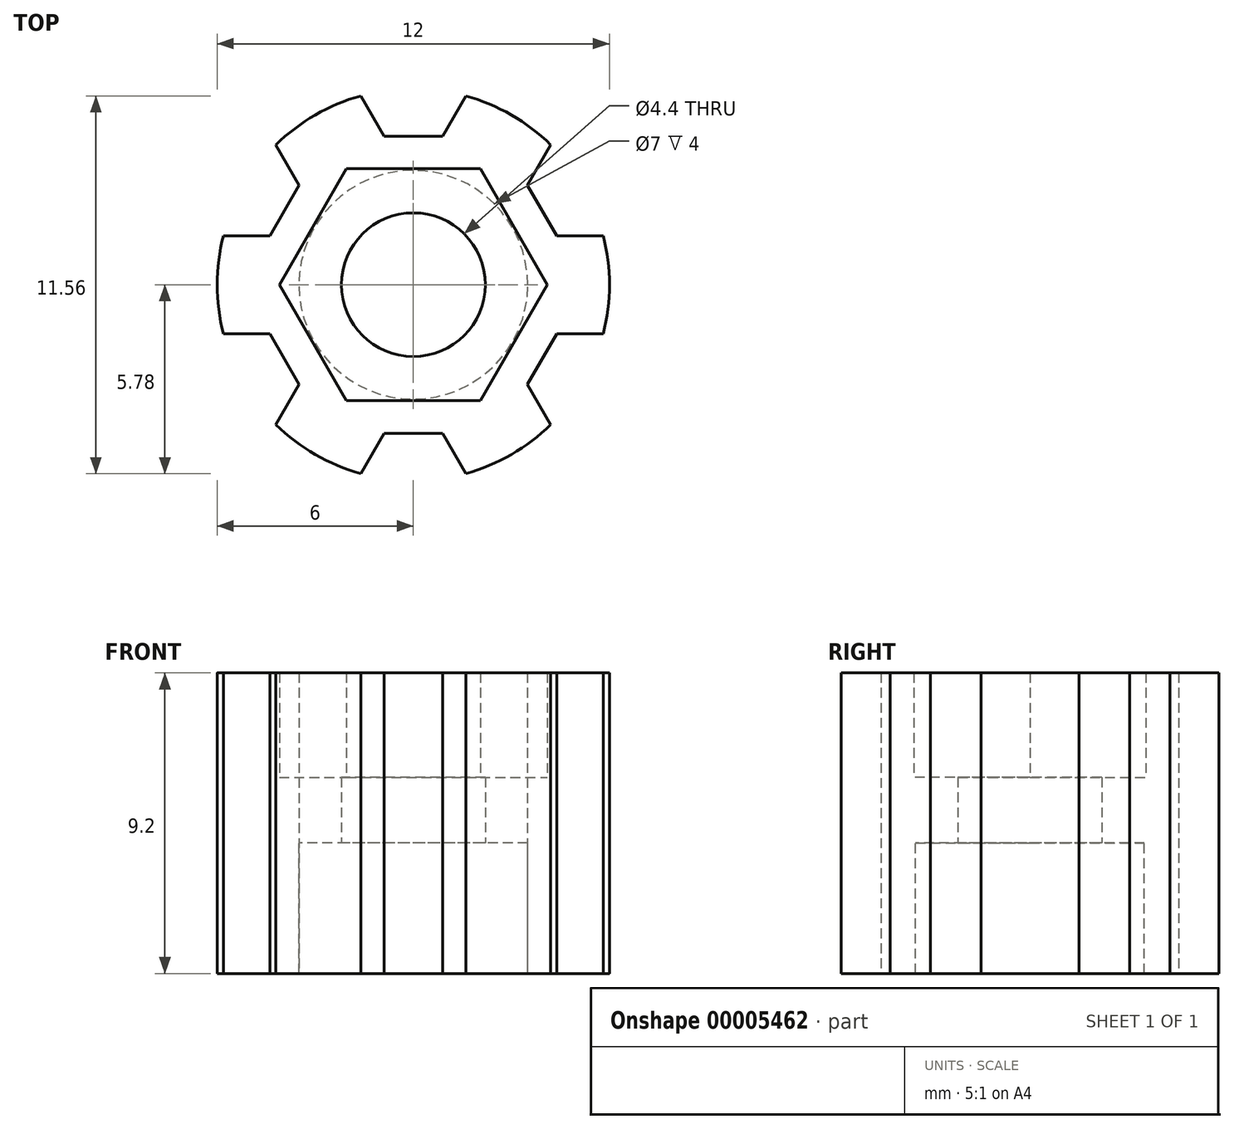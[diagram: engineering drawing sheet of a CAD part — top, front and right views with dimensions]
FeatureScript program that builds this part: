
annotation { "Feature Type Name" : "Feature", "Feature Type Description" : "" }
export const myFeature = defineFeature(function(context is Context, id is Id, definition is map)
    precondition{}
    {
        {
            var Q0;
            Q0=qCreatedBy(makeId("Top.planeOp"),FACE);
            var sketch = newSketch(context, id + "F0", { "sketchPlane" : qUnion([Q0])});
            skCircle(sketch, "E0.cCircle", {"center": v(0, 0) * mm, "radius": 3.55 * mm, "construction": true});
            skLineSegment(sketch, "E0.0", {"start": v(-2.05, 3.55) * mm, "end": v(2.05, 3.55) * mm});
            skLineSegment(sketch, "E0.1", {"start": v(2.05, 3.55) * mm, "end": v(4.1, 0) * mm});
            skLineSegment(sketch, "E0.2", {"start": v(4.1, 0) * mm, "end": v(2.05, -3.55) * mm});
            skLineSegment(sketch, "E0.3", {"start": v(2.05, -3.55) * mm, "end": v(-2.05, -3.55) * mm});
            skLineSegment(sketch, "E0.4", {"start": v(-2.05, -3.55) * mm, "end": v(-4.1, 0) * mm});
            skLineSegment(sketch, "E0.5", {"start": v(-4.1, 0) * mm, "end": v(-2.05, 3.55) * mm});
            skPoint(sketch, "E0.0.midPoint", {"position": v(0, 3.55) * mm});
            skCircle(sketch, "E1", {"center": v(0, 0) * mm, "radius": 2.2 * mm});
            skCircle(sketch, "E2", {"center": v(0, 0) * mm, "radius": 6 * mm});
            skLineSegment(sketch, "E3", {"start": v(-1.6, 5.78) * mm, "end": v(-0.9, 4.55) * mm});
            skLineSegment(sketch, "E4", {"start": v(-0.9, 4.55) * mm, "end": v(0.9, 4.55) * mm});
            skLineSegment(sketch, "E5", {"start": v(0.9, 4.55) * mm, "end": v(1.6, 5.78) * mm});
            skLineSegment(sketch, "E6", {"start": v(-2.05, 3.55) * mm, "end": v(-3, 5.2) * mm, "construction": true});
            skLineSegment(sketch, "E7.1.0", {"start": v(-5.8, 1.5) * mm, "end": v(-4.39, 1.5) * mm});
            skLineSegment(sketch, "E7.1.1", {"start": v(-4.39, 1.5) * mm, "end": v(-3.5, 3.05) * mm});
            skLineSegment(sketch, "E7.1.2", {"start": v(-3.5, 3.05) * mm, "end": v(-4.2, 4.28) * mm});
            skLineSegment(sketch, "E7.2.0", {"start": v(-4.2, -4.28) * mm, "end": v(-3.5, -3.05) * mm});
            skLineSegment(sketch, "E7.2.1", {"start": v(-3.5, -3.05) * mm, "end": v(-4.39, -1.5) * mm});
            skLineSegment(sketch, "E7.2.2", {"start": v(-4.39, -1.5) * mm, "end": v(-5.8, -1.5) * mm});
            skLineSegment(sketch, "E7.3.0", {"start": v(1.6, -5.78) * mm, "end": v(0.9, -4.55) * mm});
            skLineSegment(sketch, "E7.3.1", {"start": v(0.9, -4.55) * mm, "end": v(-0.9, -4.55) * mm});
            skLineSegment(sketch, "E7.3.2", {"start": v(-0.9, -4.55) * mm, "end": v(-1.6, -5.78) * mm});
            skLineSegment(sketch, "E7.4.0", {"start": v(5.8, -1.5) * mm, "end": v(4.39, -1.5) * mm});
            skLineSegment(sketch, "E7.4.1", {"start": v(4.39, -1.5) * mm, "end": v(3.5, -3.05) * mm});
            skLineSegment(sketch, "E7.4.2", {"start": v(3.5, -3.05) * mm, "end": v(4.2, -4.28) * mm});
            skLineSegment(sketch, "E7.5.0", {"start": v(4.2, 4.28) * mm, "end": v(3.5, 3.05) * mm});
            skLineSegment(sketch, "E7.5.1", {"start": v(3.5, 3.05) * mm, "end": v(4.39, 1.5) * mm});
            skLineSegment(sketch, "E7.5.2", {"start": v(4.39, 1.5) * mm, "end": v(5.8, 1.5) * mm});
            skSolve(sketch);
        }
        {
            var Q0;
            Q0=makeQuery(id+"F0.imprint","IMPRINT",FACE,{"disambiguationData":[TD([[makeQuery(id+"F0.imprint","IMPRINT",EDGE,{"derivedFrom":sQuery(id+"F0.wireOp",EDGE,"E0.0")}),1.0]])]});
            extrude(context, id + "F1", {"entities" : qUnion([Q0]), "depth" : 4.2 * mm});
        }
        {
            var Q0;
            Q0=makeQuery(id+"F0.imprint","IMPRINT",FACE,{"disambiguationData":[TD([[makeQuery(id+"F0.imprint","IMPRINT",EDGE,{"derivedFrom":sQuery(id+"F0.wireOp",EDGE,"E0.0")}),-1.0]])]});
            extrude(context, id + "F2", {"entities" : qUnion([Q0]), "operationType" : NewBodyOperationType.ADD, "depth" : 1 * mm});
        }
        {
            var Q0;
            Q0=qCreatedBy(makeId("Top.planeOp"),FACE);
            var sketch = newSketch(context, id + "F3", { "sketchPlane" : qUnion([Q0])});
            skCircle(sketch, "E8.0", {"center": v(0, 0) * mm, "radius": 2.2 * mm});
            skCircle(sketch, "E9", {"center": v(0, 0) * mm, "radius": 3.5 * mm});
            skArc(sketch, "E10.0", {"start": v(5.8, -1.5) * mm, "mid": v(6, 0) * mm, "end": v(5.8, 1.5) * mm});
            skLineSegment(sketch, "E10.1", {"start": v(5.8, -1.5) * mm, "end": v(4.39, -1.5) * mm});
            skLineSegment(sketch, "E10.2", {"start": v(4.39, -1.5) * mm, "end": v(3.5, -3.05) * mm});
            skLineSegment(sketch, "E10.3", {"start": v(3.5, -3.05) * mm, "end": v(4.2, -4.28) * mm});
            skArc(sketch, "E10.4", {"start": v(1.6, -5.78) * mm, "mid": v(3, -5.2) * mm, "end": v(4.2, -4.28) * mm});
            skLineSegment(sketch, "E10.5", {"start": v(1.6, -5.78) * mm, "end": v(0.9, -4.55) * mm});
            skLineSegment(sketch, "E10.6", {"start": v(0.9, -4.55) * mm, "end": v(-0.9, -4.55) * mm});
            skLineSegment(sketch, "E10.7", {"start": v(-0.9, -4.55) * mm, "end": v(-1.6, -5.78) * mm});
            skArc(sketch, "E10.8", {"start": v(-4.2, -4.28) * mm, "mid": v(-3, -5.2) * mm, "end": v(-1.6, -5.78) * mm});
            skLineSegment(sketch, "E10.9", {"start": v(-4.2, -4.28) * mm, "end": v(-3.5, -3.05) * mm});
            skLineSegment(sketch, "E10.10", {"start": v(-3.5, -3.05) * mm, "end": v(-4.39, -1.5) * mm});
            skLineSegment(sketch, "E10.11", {"start": v(-4.39, -1.5) * mm, "end": v(-5.8, -1.5) * mm});
            skArc(sketch, "E10.12", {"start": v(-5.8, 1.5) * mm, "mid": v(-6, 0) * mm, "end": v(-5.8, -1.5) * mm});
            skLineSegment(sketch, "E10.13", {"start": v(-5.8, 1.5) * mm, "end": v(-4.39, 1.5) * mm});
            skLineSegment(sketch, "E10.14", {"start": v(-4.39, 1.5) * mm, "end": v(-3.5, 3.05) * mm});
            skLineSegment(sketch, "E10.15", {"start": v(-3.5, 3.05) * mm, "end": v(-4.2, 4.28) * mm});
            skArc(sketch, "E10.16", {"start": v(-1.6, 5.78) * mm, "mid": v(-3, 5.2) * mm, "end": v(-4.2, 4.28) * mm});
            skLineSegment(sketch, "E10.17", {"start": v(-1.6, 5.78) * mm, "end": v(-0.9, 4.55) * mm});
            skLineSegment(sketch, "E10.18", {"start": v(-0.9, 4.55) * mm, "end": v(0.9, 4.55) * mm});
            skLineSegment(sketch, "E10.19", {"start": v(0.9, 4.55) * mm, "end": v(1.6, 5.78) * mm});
            skArc(sketch, "E10.20", {"start": v(4.2, 4.28) * mm, "mid": v(3, 5.2) * mm, "end": v(1.6, 5.78) * mm});
            skLineSegment(sketch, "E10.21", {"start": v(4.2, 4.28) * mm, "end": v(3.5, 3.05) * mm});
            skLineSegment(sketch, "E10.22", {"start": v(3.5, 3.05) * mm, "end": v(4.39, 1.5) * mm});
            skLineSegment(sketch, "E10.23", {"start": v(4.39, 1.5) * mm, "end": v(5.8, 1.5) * mm});
            skSolve(sketch);
        }
        {
            var Q0;
            Q0=makeQuery(id+"F3.imprint","IMPRINT",FACE,{"disambiguationData":[TD([[makeQuery(id+"F3.imprint","IMPRINT",EDGE,{"derivedFrom":sQuery(id+"F3.wireOp",EDGE,"E9")}),-1.0]])]});
            extrude(context, id + "F4", {"entities" : qUnion([Q0]), "oppositeDirection" : true, "depth" : 5 * mm});
        }
        {
            var Q0;
            Q0=makeQuery(id+"F3.imprint","IMPRINT",FACE,{"disambiguationData":[TD([[makeQuery(id+"F3.imprint","IMPRINT",EDGE,{"derivedFrom":sQuery(id+"F3.wireOp",EDGE,"E8.0")}),-1.0]])]});
            extrude(context, id + "F5", {"entities" : qUnion([Q0]), "operationType" : NewBodyOperationType.ADD, "oppositeDirection" : true, "depth" : 1 * mm});
        }
    });
